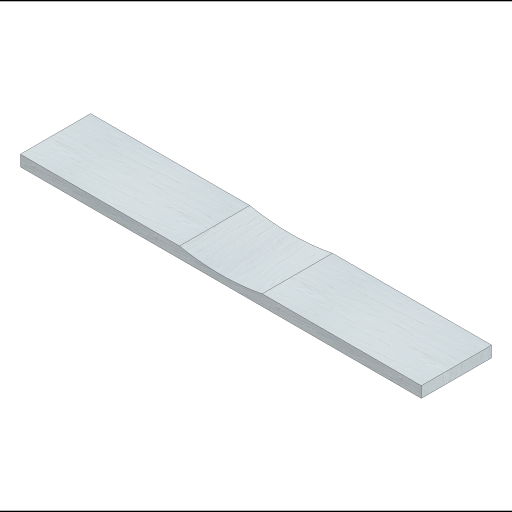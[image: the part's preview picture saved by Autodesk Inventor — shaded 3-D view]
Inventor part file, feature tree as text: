
AUTODESK INVENTOR PART (.ipt)
format: ipt  version: 2023 (Build 270158000, 158)  size: 162,304 bytes
history: native  units: in
note: dims shown in document units (in); Inventor stores cm internally (conversion verified against a paired STEP export)
features: extrude x2, sketch x2
ambient origin geometry x8: Origin, YZ Plane, XZ Plane, XY Plane, X Axis, Y Axis, Z Axis, Center Point
bodies: Solid1 (feature_tree)
feature tree (4):
  extrude  "Extrusion1"  Depth=0.47in
  extrude  "Extrusion2"  Depth=3.0in
  sketch  "Sketch1"  dims[d0=17.123in d1=0.47in]
  sketch  "Sketch2"  dims[d2=3.0in d3=0.0in d4=18.0in d5=8.825in d6=8.5615in d7=0.0in d8=0.0in]
